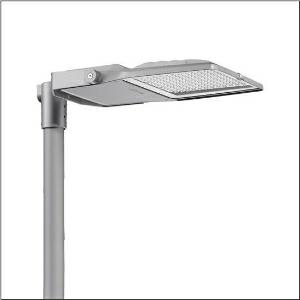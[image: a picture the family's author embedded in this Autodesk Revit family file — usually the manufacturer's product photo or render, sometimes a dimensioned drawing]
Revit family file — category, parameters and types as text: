
# Revit family: floodlight_fl_21_iq_midi___pl43_5xa7781f2a3a_7a49
name_source: partatom
category: Lighting Fixtures
units: mm (PartAtom-declared; Revit-internal decimal feet)

## family parameters
Cut with Voids When Loaded = No
Host = Face
Light Source = No
Part Type = Normal
Room Calculation Point = No
Round Connector Dimension = Use Diameter
Shared = No

## types (1)
- --- (1 x LED, 36680 lm, 270.2 W, 3000K)
    Apparent Load = 270 VA
    CIE Flux Codes = 27 78 99 100 100
    Color Rendering = 70
    Color Temperature = 3000K
    Default Elevation = 1800 mm
    Description = Floodlight FL 21 iQ midi, floodlight, primary light control with lens, of PMMA, primary optical cover: protective disc, of toughened safety glass, transparent, light distribution: PL43, light emission: direct distribution, installation type: surface-mounted, LED, High Power LED, rated luminous flux: 36.680lm, luminous efficacy: 136lm/W, light colour: 730, colour temperature: 3000K, control gear: iQ Comfort/DALI, control: optimised constant luminous flux control (CLO 2.0), Desk-Remote (wireless, voltage-free reading and setting of iQ features in the workshop via application-optimized NFC function/RFID function), Light-Fading, Smart-Wire, Night-Set, Lumen-Switch, Temp-Guard, Auto-Match, with terminal, 6-pole, mains connection: 220..240V, AC, 50/60Hz, start of lifetime: 270W, end of service life: 287W, reduction: 117W, luminaire housing, of diecast aluminium, powder-coated, Siteco® metallic grey (DB 702S), corrosivity category C5 mid according to DIN EN ISO 12944, suitable for swimming pools, chlorine-resistant, sealing non-destructively replaceable, please order mast flange separately, mast bracket, of steel, galvanised, powder-coated, Siteco® metallic grey (DB 702S), protection rating (complete): IP66, insulation class (complete): insulation class II (safety insulation), certification: CE, ENEC, VDE, protection symbol: D, impact resistance: IK08, permissible operating ambient temperature: -40..+40°C, permissible operating ambient temperature for outdoor applications: -40..+50°C, standard: DIN EN 12944, LABS conformity tested according to VDMA 24364:2018-05, packaging unit: 1 piece

Light Distribution: PL43
    Height = 76 mm
    Lamp = 1 x LED
    Lamp Light Flux = 36680 lm
    Lamp Power = 270.2 W
    Lamp count = 1
    Length = 657 mm
    Luminous efficacy = 136 lm/W
    Manufacturer = Siteco
    ModVariant = No
    Model = 5XA7781F2A3A
    Number of Poles = 1
    OnlyDefault = Yes
    Power Factor = 1
    Product Name = Floodlight FL 21 iQ midi | PL43
    Product group = floodlight | pylon annexe
    ProductGroupID = 6200
    Protection Class = Protection class II
    Protection Degree = IP 66
    RLX_Detail_Level = 1
    RLX_Emergency_Light_Flux = 0 lm
    RLX_Emergency_Type = 0
    RLX_Emergency_Type_DB = No
    RlxData = <blob elided: 153673 chars, md5=f5af869e>
    Socket = socket
    Standby Power = 0 W
    System Light Flux = 36680 lm
    System Power = 270 W
    Type Comments = factory setting: luminous flux: 100 % | dim-lin: 254 | 620 mA
    Type Image = l_1007123.jpg
    URL = http://relux.com
    VarID = @adj_104888
    Voltage = 0 V
    Weight = 0.00 kg
    Width = 442 mm

## geometry (parser evidence)
native form markers: Blend x4, Sweep x13
no freeform markers — native parametric forms only
